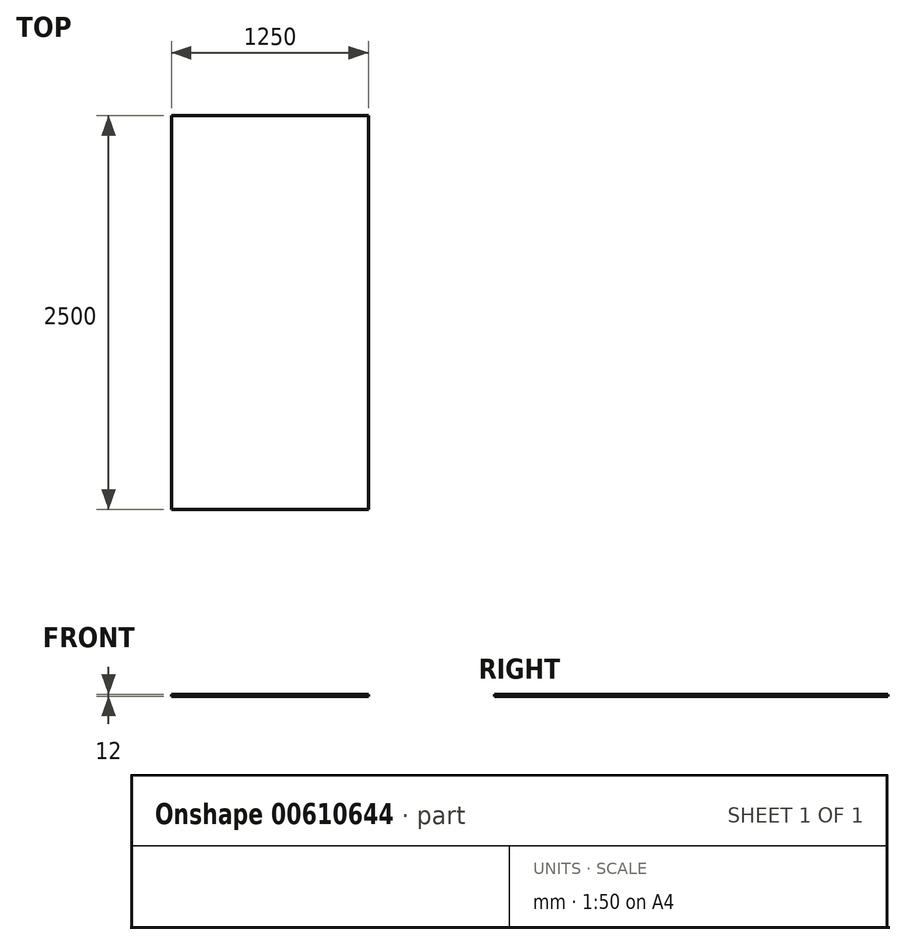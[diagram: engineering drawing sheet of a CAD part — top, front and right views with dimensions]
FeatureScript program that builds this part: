
annotation { "Feature Type Name" : "Feature", "Feature Type Description" : "" }
export const myFeature = defineFeature(function(context is Context, id is Id, definition is map)
    precondition{}
    {
        {
            var Q0;
            Q0=qCreatedBy(makeId("Top.planeOp"),FACE);
            var sketch = newSketch(context, id + "F0", { "sketchPlane" : qUnion([Q0])});
            skLineSegment(sketch, "E0.bottom", {"start": v(-1083.84, 2467.55) * mm, "end": v(166.16, 2467.55) * mm});
            skLineSegment(sketch, "E0.top", {"start": v(-1083.84, -32.45) * mm, "end": v(166.16, -32.45) * mm});
            skLineSegment(sketch, "E0.left", {"start": v(-1083.84, 2467.55) * mm, "end": v(-1083.84, -32.45) * mm});
            skLineSegment(sketch, "E0.right", {"start": v(166.16, 2467.55) * mm, "end": v(166.16, -32.45) * mm});
            skSolve(sketch);
        }
        {
            var Q0;
            Q0 = qSketchRegion(id + "F0", true);
            extrude(context, id + "F1", {"entities" : qUnion([Q0]), "depth" : 12 * mm, "offsetDistance" : 25 * mm});
        }
    });
